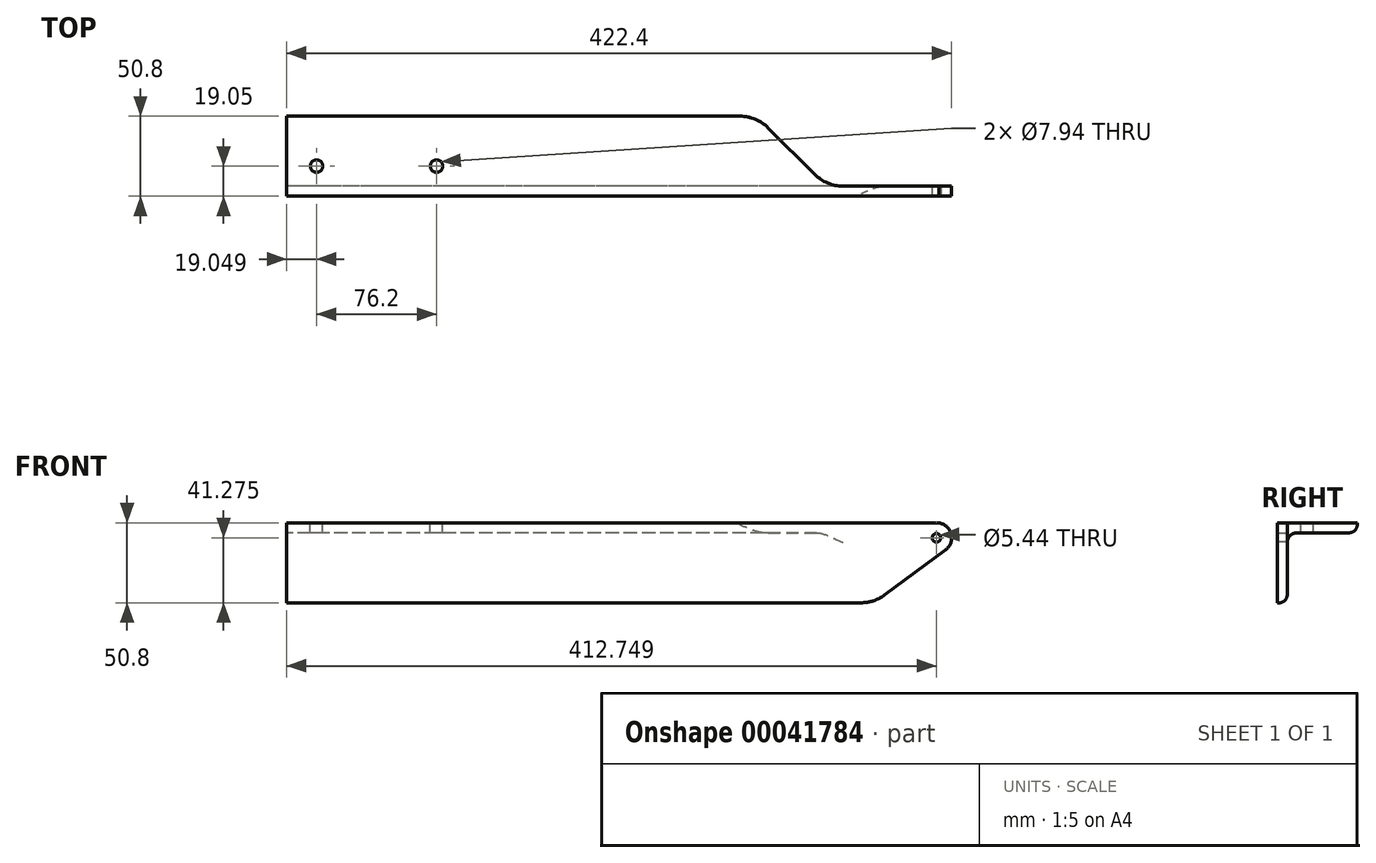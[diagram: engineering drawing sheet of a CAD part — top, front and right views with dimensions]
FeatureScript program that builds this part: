
annotation { "Feature Type Name" : "Feature", "Feature Type Description" : "" }
export const myFeature = defineFeature(function(context is Context, id is Id, definition is map)
    precondition{}
    {
        {
            var Q0;
            Q0=qCreatedBy(makeId("Right.planeOp"),FACE);
            var sketch = newSketch(context, id + "F0", { "sketchPlane" : qUnion([Q0])});
            skLineSegment(sketch, "E0.bottom", {"start": v(0, 0) * mm, "end": v(50.8, 0) * mm});
            skLineSegment(sketch, "E0.top", {"start": v(0, -50.8) * mm, "end": v(1.27, -50.8) * mm});
            skLineSegment(sketch, "E0.left", {"start": v(0, 0) * mm, "end": v(0, -50.8) * mm});
            skLineSegment(sketch, "E0.right", {"start": v(50.8, 0) * mm, "end": v(50.8, -1.27) * mm});
            skLineSegment(sketch, "E1.0", {"start": v(12.7, -6.35) * mm, "end": v(45.72, -6.35) * mm});
            skLineSegment(sketch, "E1.1", {"start": v(6.35, -12.7) * mm, "end": v(6.35, -45.72) * mm});
            skPoint(sketch, "E2.visualSharp", {"position": v(50.8, -6.35) * mm});
            skArc(sketch, "E2.filletArc", {"start": v(45.72, -6.35) * mm, "mid": v(49.31, -4.86) * mm, "end": v(50.8, -1.27) * mm});
            skPoint(sketch, "E3.visualSharp", {"position": v(6.35, -50.8) * mm});
            skArc(sketch, "E3.filletArc", {"start": v(1.27, -50.8) * mm, "mid": v(4.86, -49.31) * mm, "end": v(6.35, -45.72) * mm});
            skPoint(sketch, "E4.visualSharp", {"position": v(6.35, -6.35) * mm});
            skArc(sketch, "E4.filletArc", {"start": v(12.7, -6.35) * mm, "mid": v(8.2, -8.2) * mm, "end": v(6.35, -12.7) * mm});
            skSolve(sketch);
        }
        {
            var Q0;
            Q0 = qSketchRegion(id + "F0", true);
            extrude(context, id + "F1", {"entities" : qUnion([Q0]), "endBound" : BoundingType.SYMMETRIC, "depth" : 422.4 * mm});
        }
        {
            var Q0;
            Q0=makeQuery(id+"F1.opExtrude","SWEPT_FACE",FACE,{"disambiguationData":[OSD([sQuery(id+"F0.wireOp",EDGE,"E0.bottom")])]});
            var sketch = newSketch(context, id + "F2", { "sketchPlane" : qUnion([Q0])});
            skLineSegment(sketch, "E5.0", {"start": v(211.2, 19.05) * mm, "end": v(-211.2, 19.05) * mm, "construction": true});
            skLineSegment(sketch, "E6.0", {"start": v(-192.15, 0) * mm, "end": v(-192.15, 50.8) * mm, "construction": true});
            skLineSegment(sketch, "E7.0", {"start": v(-115.95, 0) * mm, "end": v(-115.95, 50.8) * mm, "construction": true});
            skCircle(sketch, "E8", {"center": v(-192.15, 19.05) * mm, "radius": 3.97 * mm});
            skCircle(sketch, "E9", {"center": v(-115.95, 19.05) * mm, "radius": 3.97 * mm});
            skSolve(sketch);
        }
        {
            var Q0;
            Q0 = qSketchRegion(id + "F2", true);
            extrude(context, id + "F3", {"entities" : qUnion([Q0]), "operationType" : NewBodyOperationType.REMOVE, "oppositeDirection" : true, "depth" : 25.4 * mm});
        }
        {
            var Q0;
            Q0=makeQuery(id+"F1.opExtrude","SWEPT_FACE",FACE,{"disambiguationData":[OSD([sQuery(id+"F0.wireOp",EDGE,"E0.bottom")])]});
            var sketch = newSketch(context, id + "F4", { "sketchPlane" : qUnion([Q0])});
            skLineSegment(sketch, "E10.0", {"start": v(211.2, 6.35) * mm, "end": v(-211.2, 6.35) * mm, "construction": true});
            skLineSegment(sketch, "E11.0", {"start": v(-211.2, 0) * mm, "end": v(-211.2, 50.8) * mm, "construction": true});
            skLineSegment(sketch, "E12.0", {"start": v(87.25, 0) * mm, "end": v(87.25, 50.8) * mm, "construction": true});
            skLineSegment(sketch, "E13.0", {"start": v(131.7, 0) * mm, "end": v(131.7, 50.8) * mm, "construction": true});
            skLineSegment(sketch, "E14.0", {"start": v(211.2, 0) * mm, "end": v(211.2, 50.8) * mm, "construction": true});
            skLineSegment(sketch, "E15.0", {"start": v(211.2, 50.8) * mm, "end": v(-211.2, 50.8) * mm, "construction": true});
            skLineSegment(sketch, "E16", {"start": v(211.2, 6.35) * mm, "end": v(211.2, 50.8) * mm});
            skLineSegment(sketch, "E17", {"start": v(87.25, 50.8) * mm, "end": v(211.2, 50.8) * mm});
            skLineSegment(sketch, "E18", {"start": v(87.25, 50.8) * mm, "end": v(131.7, 6.35) * mm});
            skLineSegment(sketch, "E19", {"start": v(131.7, 6.35) * mm, "end": v(211.2, 6.35) * mm});
            skSolve(sketch);
        }
        {
            var Q0;
            Q0 = qSketchRegion(id + "F4", true);
            extrude(context, id + "F5", {"entities" : qUnion([Q0]), "operationType" : NewBodyOperationType.REMOVE, "endBound" : BoundingType.THROUGH_ALL, "oppositeDirection" : true, "depth" : 25.4 * mm});
        }
        {
            var Q0;
            Q0=makeQuery(id+"F5.boolean.opBoolean","COPY",EDGE,{"derivedFrom":makeQuery(id+"F5.opExtrude","SWEPT_EDGE",EDGE,{"disambiguationData":[OSD([sQuery(id+"F4.wireOp",EDGE,"E18"),sQuery(id+"F4.wireOp",EDGE,"E19")])]})});
            fillet(context, id + "F6", {"entities" : qUnion([Q0]), "radius" : 25.4 * mm, "tangentPropagation" : true, "allowEdgeOverflow" : false});
        }
        {
            var Q0;
            Q0=makeQuery(id+"F1.opExtrude","SWEPT_FACE",FACE,{"disambiguationData":[OSD([sQuery(id+"F0.wireOp",EDGE,"E0.bottom")])]});
            var sketch = newSketch(context, id + "F7", { "sketchPlane" : qUnion([Q0])});
            skLineSegment(sketch, "E20.0", {"start": v(94.69, 43.36) * mm, "end": v(124.26, 13.79) * mm});
            skLineSegment(sketch, "E21.0", {"start": v(76.73, 50.8) * mm, "end": v(-211.2, 50.8) * mm});
            skPoint(sketch, "E22.visualSharp", {"position": v(87.25, 50.8) * mm});
            skArc(sketch, "E22.filletArc", {"start": v(94.69, 43.36) * mm, "mid": v(86.45, 48.87) * mm, "end": v(76.73, 50.8) * mm});
            skLineSegment(sketch, "E23", {"start": v(76.73, 50.8) * mm, "end": v(76.73, 68.3) * mm});
            skLineSegment(sketch, "E24", {"start": v(76.73, 68.3) * mm, "end": v(108.3, 68.3) * mm});
            skLineSegment(sketch, "E25", {"start": v(108.3, 68.3) * mm, "end": v(108.3, 43.36) * mm});
            skLineSegment(sketch, "E26", {"start": v(108.3, 43.36) * mm, "end": v(94.69, 43.36) * mm});
            skSolve(sketch);
        }
        {
            var Q0;
            Q0 = qSketchRegion(id + "F7", true);
            extrude(context, id + "F8", {"entities" : qUnion([Q0]), "operationType" : NewBodyOperationType.REMOVE, "endBound" : BoundingType.THROUGH_ALL, "oppositeDirection" : true, "depth" : 25.4 * mm});
        }
        {
            var Q0;
            Q0=makeQuery(id+"F1.opExtrude","SWEPT_FACE",FACE,{"disambiguationData":[OSD([sQuery(id+"F0.wireOp",EDGE,"E0.left")])]});
            var sketch = newSketch(context, id + "F9", { "sketchPlane" : qUnion([Q0])});
            skLineSegment(sketch, "E27.0", {"start": v(-211.2, 0) * mm, "end": v(-211.2, -50.8) * mm, "construction": true});
            skLineSegment(sketch, "E28.0", {"start": v(201.55, 0) * mm, "end": v(201.55, -50.8) * mm, "construction": true});
            skLineSegment(sketch, "E29.0", {"start": v(161.93, 0) * mm, "end": v(161.93, -50.8) * mm, "construction": true});
            skLineSegment(sketch, "E30.0", {"start": v(211.2, -50.8) * mm, "end": v(-211.2, -50.8) * mm});
            skLineSegment(sketch, "E31.0", {"start": v(211.2, 0) * mm, "end": v(-211.2, 0) * mm, "construction": true});
            skLineSegment(sketch, "E32.0", {"start": v(211.2, -9.53) * mm, "end": v(-211.2, -9.53) * mm, "construction": true});
            skCircle(sketch, "E33", {"center": v(201.55, -9.52) * mm, "radius": 2.72 * mm});
            skArc(sketch, "E34", {"start": v(207.28, -17.29) * mm, "mid": v(210.72, -6.5) * mm, "end": v(201.55, 0.13) * mm});
            skLineSegment(sketch, "E35", {"start": v(161.93, -50.8) * mm, "end": v(207.28, -17.29) * mm});
            skLineSegment(sketch, "E36", {"start": v(201.55, 0) * mm, "end": v(201.55, 11.9) * mm});
            skLineSegment(sketch, "E37", {"start": v(161.93, -50.8) * mm, "end": v(161.93, -62.77) * mm});
            skLineSegment(sketch, "E38", {"start": v(201.55, 11.9) * mm, "end": v(237.1, 11.9) * mm});
            skLineSegment(sketch, "E39", {"start": v(161.93, -62.77) * mm, "end": v(237.1, -62.77) * mm});
            skLineSegment(sketch, "E40", {"start": v(237.1, -62.77) * mm, "end": v(237.1, 11.9) * mm});
            skSolve(sketch);
        }
        {
            var Q0;
            Q0 = qSketchRegion(id + "F9", true);
            extrude(context, id + "F10", {"entities" : qUnion([Q0]), "operationType" : NewBodyOperationType.REMOVE, "endBound" : BoundingType.THROUGH_ALL, "oppositeDirection" : true, "depth" : 25.4 * mm});
        }
        {
            var Q0;
            Q0=makeQuery(id+"F1.opExtrude","SWEPT_FACE",FACE,{"disambiguationData":[OSD([sQuery(id+"F0.wireOp",EDGE,"E0.left")])]});
            var sketch = newSketch(context, id + "F11", { "sketchPlane" : qUnion([Q0])});
            skLineSegment(sketch, "E41.0", {"start": v(168.65, -45.83) * mm, "end": v(207.28, -17.29) * mm});
            skLineSegment(sketch, "E42.0", {"start": v(153.56, -50.8) * mm, "end": v(-211.2, -50.8) * mm});
            skPoint(sketch, "E43.visualSharp", {"position": v(161.93, -50.8) * mm});
            skArc(sketch, "E43.filletArc", {"start": v(153.56, -50.8) * mm, "mid": v(161.5, -49.53) * mm, "end": v(168.65, -45.83) * mm});
            skLineSegment(sketch, "E44", {"start": v(153.56, -50.8) * mm, "end": v(153.56, -83.13) * mm});
            skLineSegment(sketch, "E45", {"start": v(207.28, -17.29) * mm, "end": v(207.28, -83.13) * mm});
            skLineSegment(sketch, "E46", {"start": v(207.28, -83.13) * mm, "end": v(153.56, -83.13) * mm});
            skSolve(sketch);
        }
        {
            var Q0;
            Q0 = qSketchRegion(id + "F11", true);
            extrude(context, id + "F12", {"entities" : qUnion([Q0]), "operationType" : NewBodyOperationType.REMOVE, "endBound" : BoundingType.THROUGH_ALL, "oppositeDirection" : true, "depth" : 25.4 * mm});
        }
    });
